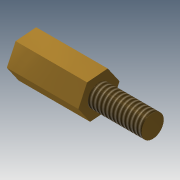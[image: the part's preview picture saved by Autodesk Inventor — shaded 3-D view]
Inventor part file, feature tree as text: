
AUTODESK INVENTOR PART (.ipt)
format: ipt  version: 2014 SP1 (Build 180222100, 222)  size: 103,424 bytes
history: native  units: mm
features: sketch x3, extrude x2, thread x1, hole x1
ambient origin geometry x8: Origin, YZ Plane, XZ Plane, XY Plane, X Axis, Y Axis, Z Axis, Center Point
bodies: Solid1 (feature_tree)
feature tree (7):
  extrude  "Extrusion1"  Depth=8.0mm TaperAngle=0.0deg
  extrude  "Extrusion2"  Depth=6.0mm TaperAngle=0.0deg
  thread  "Thread1"  [1 undecoded]
  hole  "Hole1"  [1 undecoded]
  sketch  "Sketch1"  dims[d0=2.0mm d1=8.0mm d2=0.0mm]
  sketch  "Sketch2"  dims[d3=2.5mm d4=6.0mm d5=0.0mm d6=10.0mm d7=0.0mm]
  sketch  "Sketch3"  dims[d8=2.013mm d9=6.0mm d10=4.0mm d11=2.0mm d12=90.0deg d13=5.0mm d14=20.594885mm]
note: 2 required parameter values undecoded (feature->parameter linkage not recoverable at this tier; creation-order binding heuristic only, values carry confidence <= 0.55)
